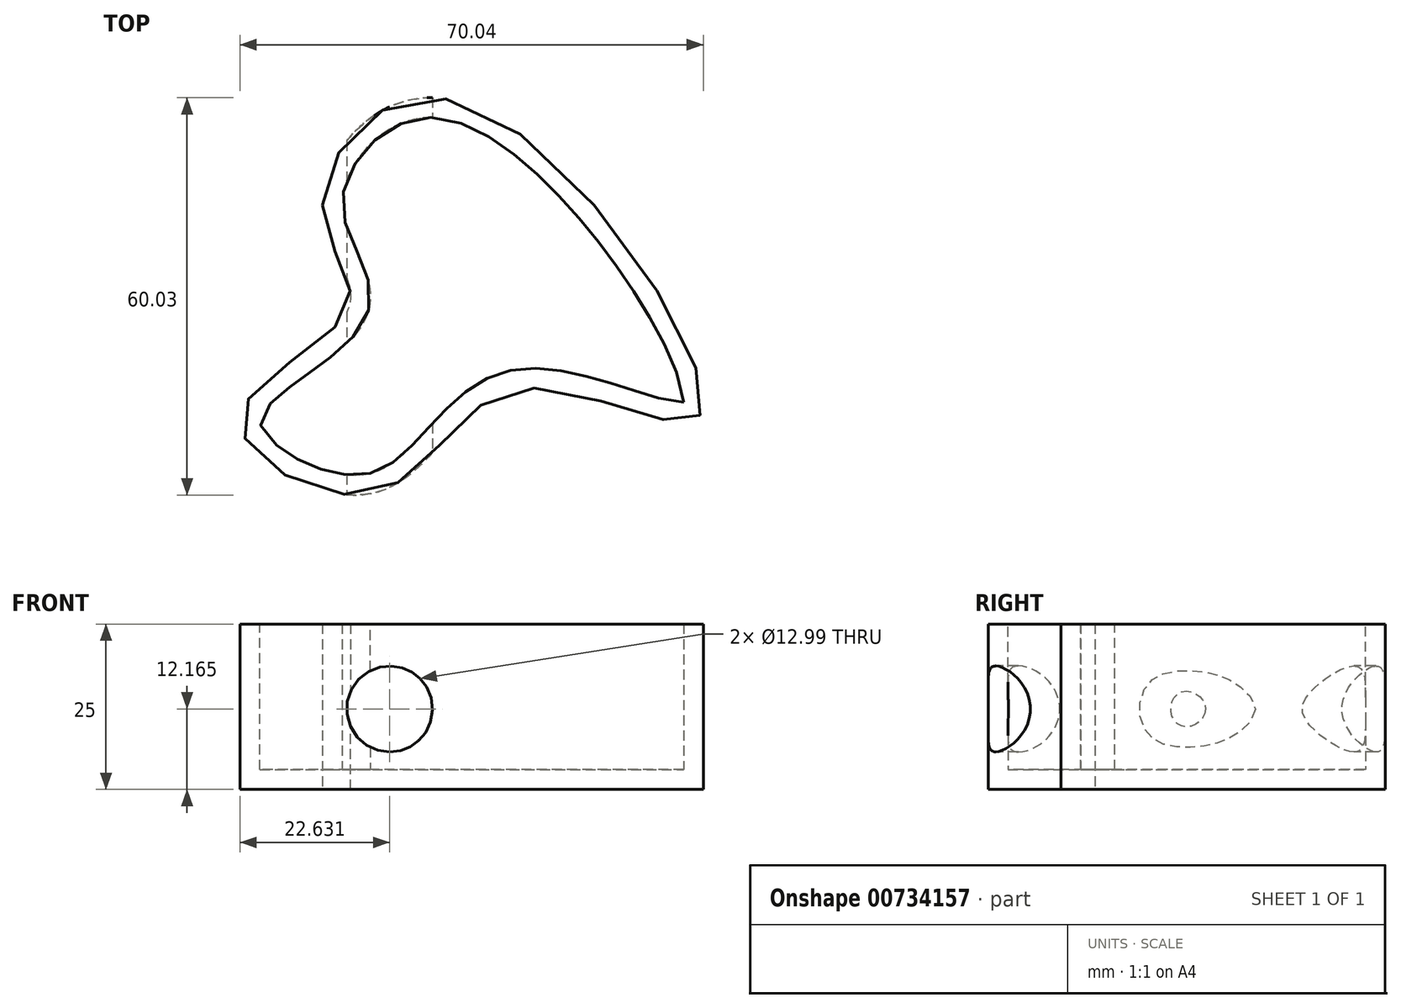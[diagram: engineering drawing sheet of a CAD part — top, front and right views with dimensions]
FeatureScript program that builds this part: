
annotation { "Feature Type Name" : "Feature", "Feature Type Description" : "" }
export const myFeature = defineFeature(function(context is Context, id is Id, definition is map)
    precondition{}
    {
        {
            var Q0;
            Q0=qCreatedBy(makeId("Top.planeOp"),FACE);
            var sketch = newSketch(context, id + "F0", { "sketchPlane" : qUnion([Q0])});
            skFitSpline(sketch, "E0", {"points": [v(-36.86, 15.84) * mm, v(-16.43, 31.53) * mm, v(20.28, -15.84) * mm, v(-7.25, -12) * mm, v(-29.16, -27.68) * mm, v(-49.3, -16.43) * mm, v(-33, 0) * mm, v(-36.86, 15.84) * mm]});
            skSolve(sketch);
        }
        {
            var Q0;
            Q0=makeQuery(id+"F0.imprint","IMPRINT",FACE,{"disambiguationData":[TD([[makeQuery(id+"F0.imprint","IMPRINT",EDGE,{"derivedFrom":sQuery(id+"F0.wireOp",EDGE,"E0")}),-1.0]])]});
            var Q1;
            Q1 = qSketchRegion(id + "FVsPAmSxcnzHajj_1", true);
            extrude(context, id + "F1", {"entities" : qUnion([Q0, Q1]), "depth" : 25 * mm, "offsetDistance" : 25 * mm});
        }
        {
            var Q0;
            Q0=makeQuery(id+"F1.opExtrude","CAP_FACE",FACE,{"disambiguationData":[OSD([sQuery(id+"F0.wireOp",EDGE,"E0")])],"isStart":false});
            shell(context, id + "F2", {"entities" : qUnion([Q0]), "thickness" : 3 * mm});
        }
        {
            var Q0;
            Q0=qCreatedBy(makeId("Front.planeOp"),FACE);
            cPlane(context, id + "F3", {"entities" : qUnion([Q0]), "cplaneType" : CPlaneType.OFFSET, "offset" : 30 * mm, "width" : 150 * mm, "height" : 150 * mm});
        }
        {
            var Q0;
            Q0=qCreatedBy(id+"F3.planeOp",FACE);
            var sketch = newSketch(context, id + "F4", { "sketchPlane" : qUnion([Q0])});
            skLineSegment(sketch, "E1", {"start": v(-26.68, 24.33) * mm, "end": v(-26.68, 0) * mm});
            skCircle(sketch, "E2", {"center": v(-26.68, 12.17) * mm, "radius": 6.5 * mm});
            skSolve(sketch);
        }
        {
            var Q0;
            Q0 = qSketchRegion(id + "F4", true);
            extrude(context, id + "F5", {"entities" : qUnion([Q0]), "operationType" : NewBodyOperationType.REMOVE, "endBound" : BoundingType.THROUGH_ALL, "oppositeDirection" : true, "depth" : 25 * mm, "offsetDistance" : 25 * mm});
        }
    });
